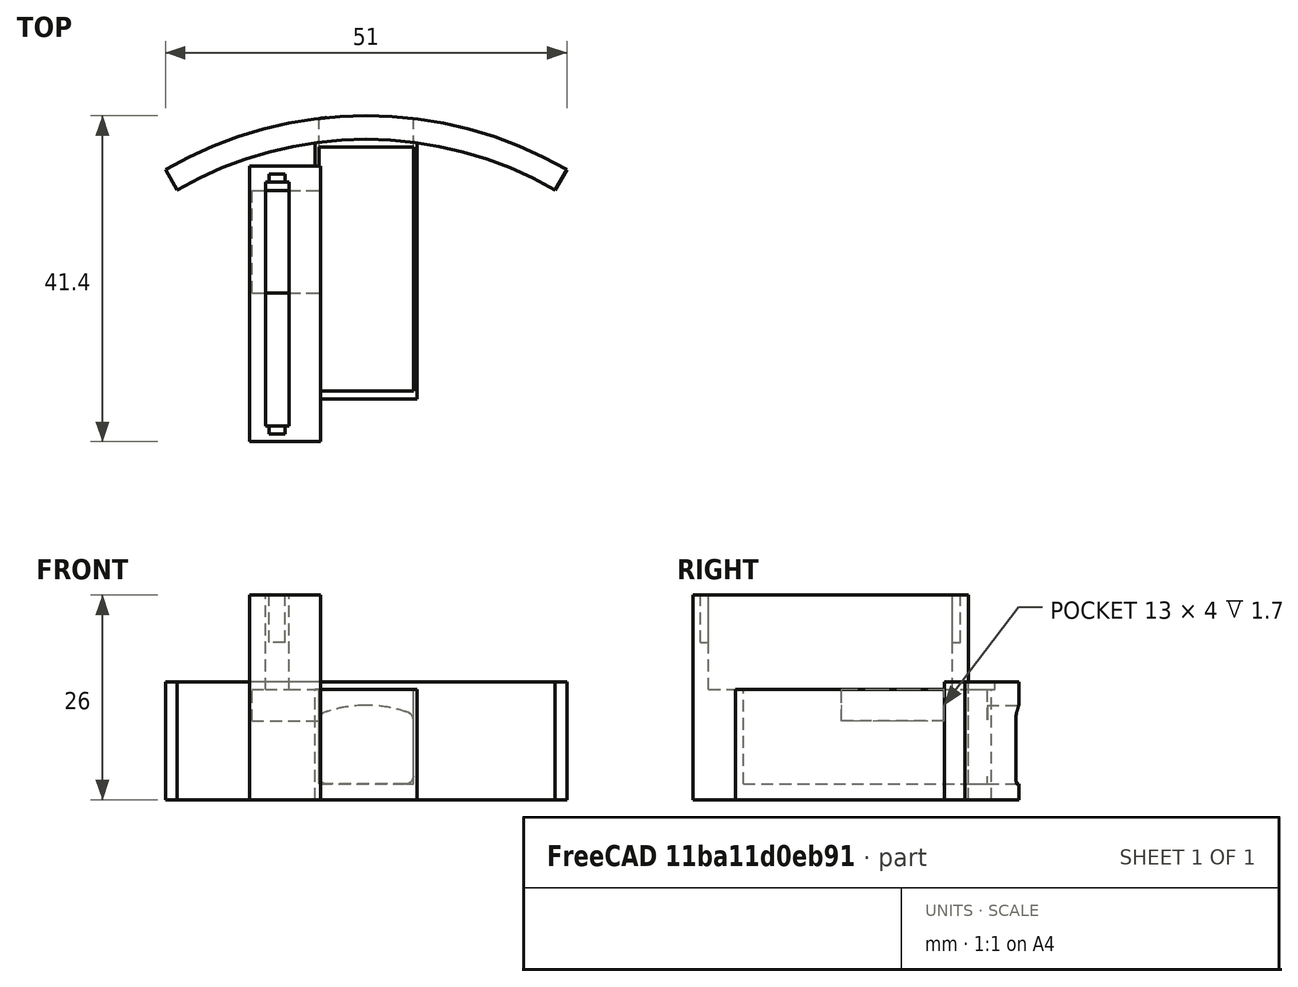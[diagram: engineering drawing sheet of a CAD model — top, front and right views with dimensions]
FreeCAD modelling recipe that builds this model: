
FCSTD DOCUMENT  (FreeCAD 0.16R4924 (Git))
Label: interior_servo_bay_v4p2
License: All rights reserved
LicenseURL: http://en.wikipedia.org/wiki/All_rights_reserved
objects: Part::Cut×6, Part::Box×6, Part::MultiFuse×3, Part::Cylinder×2, Part::Feature×2, Part::Extrusion×2, Part::Thickness×1
note: 22 computed .brp shape members not serialized (recipe doc carries the construction recipe); baked Part::Feature solids carry a one-line shape summary decoded from their .brp

FEATURE [Part::Cylinder] Cylinder  label="bottle_wall"
  Angle = 60
  Height = 15
  Placement = pos=(8.5,-7,0) rot=(0,0,1;1.0472rad)
  Radius = 51
FEATURE [Part::Cylinder] Cylinder001  label="bottle_wall001"
  Angle = 60
  Height = 15
  Placement = pos=(8.5,-7,0) rot=(0,0,1;1.0472rad)
  Radius = 48
FEATURE [Part::Cut] Cut  label="bottle_wall_composite"
  Base = -> Cylinder
  Placement = pos=(0,-2,0) rot=(0,0,1;0rad)
  Tool = -> Cylinder001
FEATURE [Part::Feature] Common_cs  label="pin_cs"
  Placement = pos=(3.5,35,2) rot=(0,0,1;0rad)
  shape: bbox 10 x 2e-07 x 8 mm, 0 faces, 0 solids (baked)
FEATURE [Part::Extrusion] Extrude
  Base = -> Common_cs
  Dir = (0,5,0)
  Solid = true
FEATURE [Part::Thickness] Thickness
  Faces = -> Extrude [Face7]
  Intersection = false
  Join = 0
  Mode = 0
  SelfIntersection = false
  Value = 1
FEATURE [Part::Feature] Common_cs001  label="pin_cs001"
  Placement = pos=(3.5,35,2) rot=(0,0,1;0rad)
  shape: bbox 10 x 2e-07 x 8 mm, 0 faces, 0 solids (baked)
FEATURE [Part::Extrusion] Extrude001
  Base = -> Common_cs001
  Dir = (0,5,0)
  Solid = true
FEATURE [Part::MultiFuse] Fusion  label="bolt_bottle_side_opening"
  Placement = pos=(0,-7,1) rot=(0,0,1;0rad)
  Shapes = -> [Thickness,Extrude,Extrude001]
FEATURE [Part::Box] Box  label="pullBay"
  Height = 15
  Length = 12
  Placement = pos=(2.5,7,2) rot=(0,0,1;0rad)
  Width = 31
FEATURE [Part::Box] Box001  label="Case"
  Height = 14
  Length = 13
  Placement = pos=(2,6,0) rot=(0,0,1;0rad)
  Width = 34
FEATURE [Part::Cut] Cut001  label="cut bay from case"
  Base = -> Box001
  Tool = -> Box
FEATURE [Part::MultiFuse] Fusion001  label="wall plus case"
  Shapes = -> [Cut,Cut001]
FEATURE [Part::Cut] Cut002  label="hole cut out of case"
  Base = -> Fusion001
  Tool = -> Fusion
FEATURE [Part::Box] Box002  label="slot body"
  Height = 26
  Length = 9
  Placement = pos=(-3,5,0) rot=(0,0,1;0rad)
  Width = 35
FEATURE [Part::Box] Box003  label="slot wall cutout1"
  Height = 11.2
  Length = 2
  Placement = pos=(-0.5,6,20) rot=(0,0,1;0rad)
  Width = 33
FEATURE [Part::Cut] Cut003
  Base = -> Box002
  Tool = -> Box003
FEATURE [Part::Box] Box004  label="slot wall cutout2"
  Height = 14
  Length = 3
  Placement = pos=(-1,7,14) rot=(0,0,1;0rad)
  Width = 31
FEATURE [Part::Cut] Cut004  label="wall slot finished"
  Base = -> Cut003
  Placement = pos=(-3.3,-4.4,0) rot=(0,0,1;0rad)
  Tool = -> Box004
FEATURE [Part::MultiFuse] Fusion002
  Shapes = -> [Cut002,Cut004]
FEATURE [Part::Box] Box005  label="servo wall cutaway"
  Height = 4
  Length = 10
  Placement = pos=(-6,19.5,10) rot=(0,0,1;0rad)
  Width = 13
FEATURE [Part::Cut] Cut005
  Base = -> Fusion002
  Tool = -> Box005
